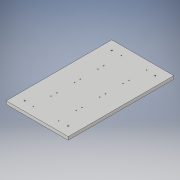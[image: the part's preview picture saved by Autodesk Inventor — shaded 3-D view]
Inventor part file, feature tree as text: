
AUTODESK INVENTOR PART (.ipt)
format: ipt  version: 2019.4 (Build 234330000, 330)  size: 140,288 bytes
history: native  units: in
note: dims shown in document units (in); Inventor stores cm internally (conversion verified against a paired STEP export)
features: sketch x3, hole x2, extrude x1
ambient origin geometry x8: Origin, YZ Plane, XZ Plane, XY Plane, X Axis, Y Axis, Z Axis, Center Point
bodies: Solid1 (feature_tree)
feature tree (6):
  extrude  "Extrusion1"  Depth=8.5in
  hole  "Hole1"  [1 undecoded]
  hole  "Hole2"  [1 undecoded]
  sketch  "Sketch1"  dims[d0=5.0in d1=8.5in]
  sketch  "Sketch2"  dims[d2=0.25in d3=0.0in d5=0.7132in]
  sketch  "Sketch5"  dims[d6=1.486in d7=0.0984in d8=0.0984in d9=1.4213in d10=0.0984in d11=2.0276in d12=0.0984in d13=1.5748in d15=1.8842in d16=0.3937in d18=0.3937in d20=0.062in d21=0.25in d22=0.1575in d23=0.0787in d24=90.0deg d25=0.1875in d26=0.8108in d36=0.75in d37=0.75in d38=0.7874in d40=7.0in d41=0.7874in d43=3.5in d46=0.097in d47=0.25in d48=0.385in d49=0.25in d50=0.5635in d51=0.1875in d52=0.8108in]
note: 2 required parameter values undecoded (feature->parameter linkage not recoverable at this tier; creation-order binding heuristic only, values carry confidence <= 0.55)
